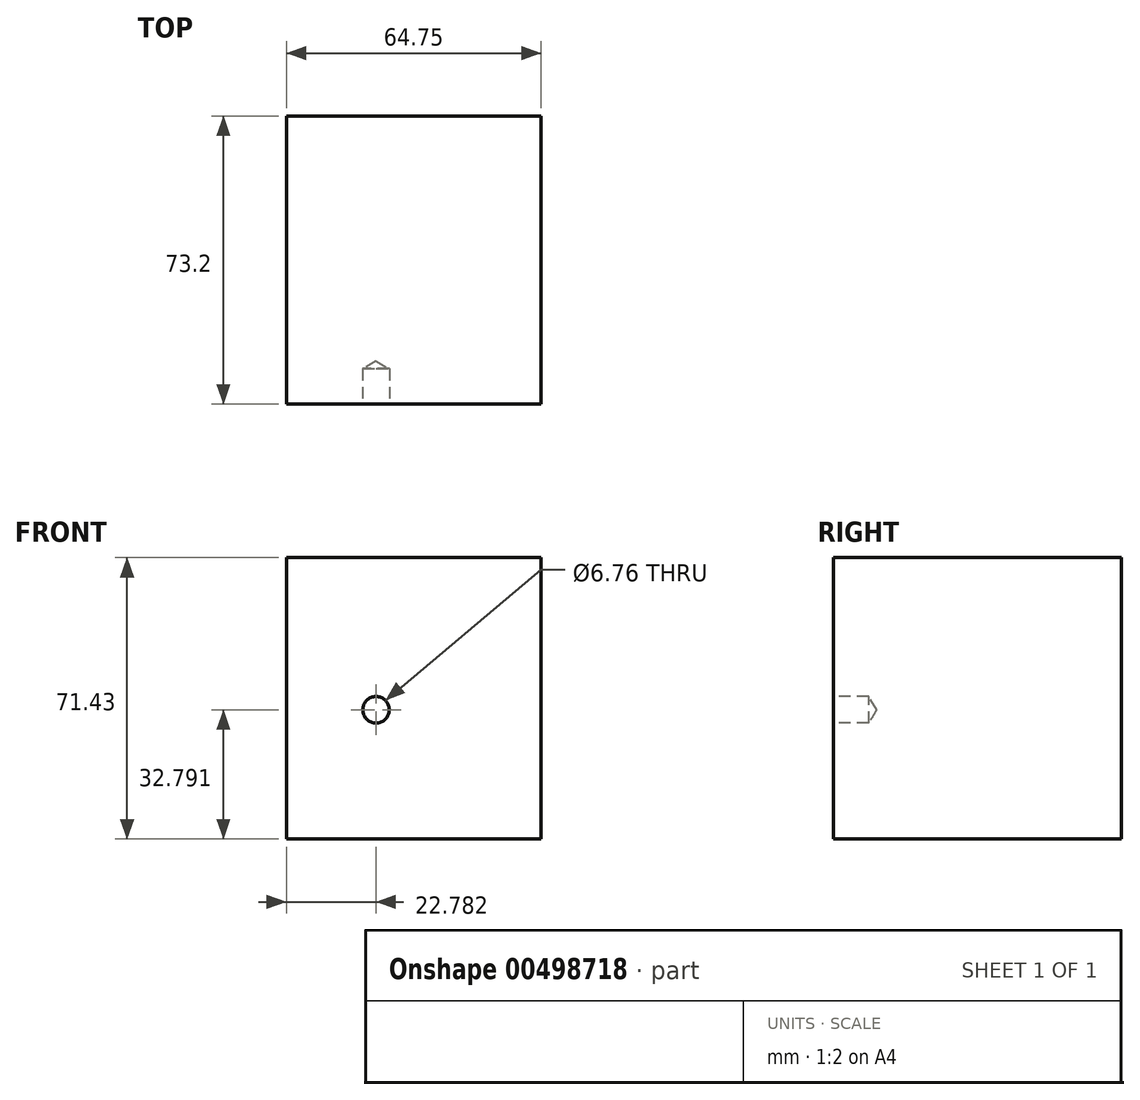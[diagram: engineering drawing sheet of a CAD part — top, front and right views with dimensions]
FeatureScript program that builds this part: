
annotation { "Feature Type Name" : "Feature", "Feature Type Description" : "" }
export const myFeature = defineFeature(function(context is Context, id is Id, definition is map)
    precondition{}
    {
        {
            var Q0;
            Q0=qCreatedBy(makeId("Front.planeOp"),FACE);
            var sketch = newSketch(context, id + "F0", { "sketchPlane" : qUnion([Q0])});
            skLineSegment(sketch, "E0.bottom", {"start": v(-99.8, -25.14) * mm, "end": v(-35.05, -25.14) * mm});
            skLineSegment(sketch, "E0.top", {"start": v(-99.8, 46.3) * mm, "end": v(-35.05, 46.3) * mm});
            skLineSegment(sketch, "E0.left", {"start": v(-99.8, -25.14) * mm, "end": v(-99.8, 46.3) * mm});
            skLineSegment(sketch, "E0.right", {"start": v(-35.05, -25.14) * mm, "end": v(-35.05, 46.3) * mm});
            skPoint(sketch, "E0.middle", {"position": v(-67.42, 10.58) * mm});
            skSolve(sketch);
        }
        {
            var Q0;
            Q0=makeQuery(id+"F0.imprint","IMPRINT",FACE,{"disambiguationData":[TD([[makeQuery(id+"F0.imprint","IMPRINT",EDGE,{"derivedFrom":sQuery(id+"F0.wireOp",EDGE,"E0.bottom")}),1.0]])]});
            extrude(context, id + "F1", {"entities" : qUnion([Q0]), "depth" : 73.2 * mm});
        }
        {
            var Q0;
            Q0=makeQuery(id+"F1.opExtrude","CAP_FACE",FACE,{"disambiguationData":[OSD([sQuery(id+"F0.wireOp",EDGE,"E0.bottom"),sQuery(id+"F0.wireOp",EDGE,"E0.top"),sQuery(id+"F0.wireOp",EDGE,"E0.left"),sQuery(id+"F0.wireOp",EDGE,"E0.right")])],"isStart":false});
            var sketch = newSketch(context, id + "F2", { "sketchPlane" : qUnion([Q0])});
            skPoint(sketch, "E1", {"position": v(-77.02, 7.65) * mm});
            skSolve(sketch);
        }
        {
            var Q0;
            Q0=sQuery(id+"F2.wireOp",VERTEX,"E1");
            var Q1;
            Q1=makeQuery(id+"F1.opExtrude","SWEPT_BODY",BODY,{"disambiguationData":[OSD([sQuery(id+"F0.wireOp",EDGE,"E0.bottom"),sQuery(id+"F0.wireOp",EDGE,"E0.top"),sQuery(id+"F0.wireOp",EDGE,"E0.left"),sQuery(id+"F0.wireOp",EDGE,"E0.right")])]});
            hole(context, id + "F3", {"style" : HoleStyle.SIMPLE, "endStyle" : HoleEndStyle.BLIND, "holeDiameter" : 6.76 * mm, "holeDepth" : 9 * mm, "isTappedThrough" : true, "tappedDepth" : 12 * mm, "tapClearance" : 3, "locations" : qUnion([Q0]), "scope" : qUnion([Q1])});
        }
    });
